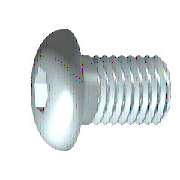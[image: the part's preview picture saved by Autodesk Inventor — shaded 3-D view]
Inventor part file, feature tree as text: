
AUTODESK INVENTOR PART (.ipt)
format: ipt  version: 2014 SP2 (Build 180246200, 246)  size: 201,216 bytes
history: native  units: mm (DEFAULTED — no unit token found)
features: sketch x2, other x1, extrude x1, plane x1
ambient origin geometry x7: Origin, YZ Plane, XY Plane, X Axis, Y Axis, Z Axis, Center Point
bodies: Solid1 (feature_tree)
feature tree (5):
  other  "Bryła"
  extrude  "Szczelina"  Depth=8.0mm
  plane  "Work Plane1"
  sketch  "Szkic1"
  sketch  "Szkic2"
